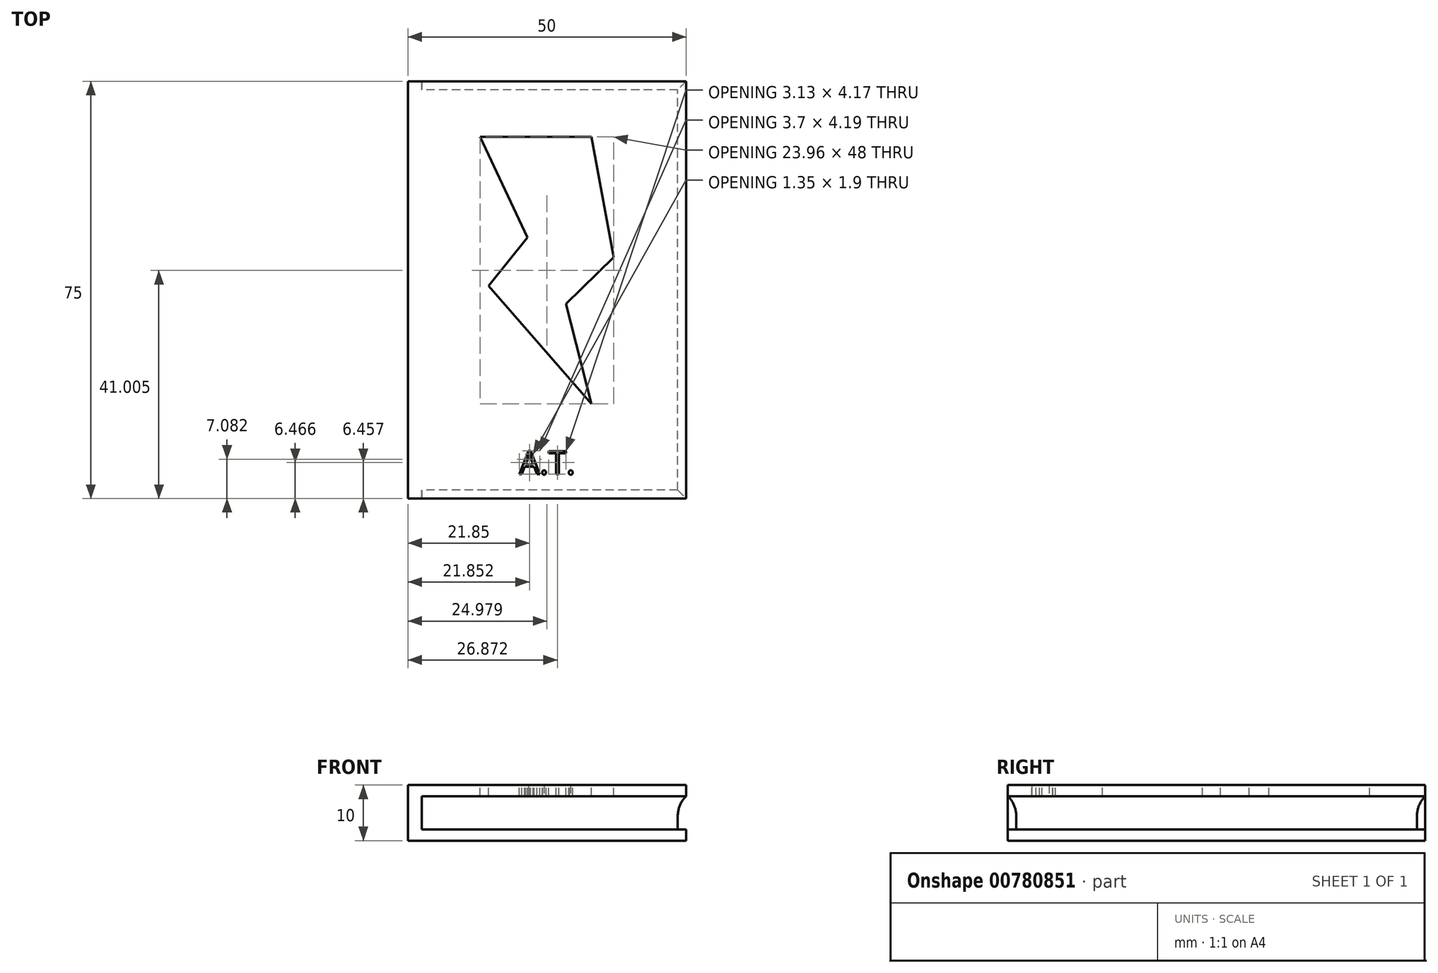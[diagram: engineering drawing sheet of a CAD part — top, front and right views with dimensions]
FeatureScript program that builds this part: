
annotation { "Feature Type Name" : "Feature", "Feature Type Description" : "" }
export const myFeature = defineFeature(function(context is Context, id is Id, definition is map)
    precondition{}
    {
        {
            var Q0;
            Q0=qCreatedBy(makeId("Top.planeOp"),FACE);
            var sketch = newSketch(context, id + "F0", { "sketchPlane" : qUnion([Q0])});
            skLineSegment(sketch, "E0.bottom", {"start": v(-61.42, 21.48) * mm, "end": v(-11.42, 21.48) * mm});
            skLineSegment(sketch, "E0.top", {"start": v(-61.42, -53.52) * mm, "end": v(-11.42, -53.52) * mm});
            skLineSegment(sketch, "E0.left", {"start": v(-61.42, 21.48) * mm, "end": v(-61.42, -53.52) * mm});
            skLineSegment(sketch, "E0.right", {"start": v(-11.42, 21.48) * mm, "end": v(-11.42, -53.52) * mm});
            skSolve(sketch);
        }
        {
            var Q0;
            Q0=makeQuery(id+"F0.imprint","IMPRINT",FACE,{"disambiguationData":[TD([[makeQuery(id+"F0.imprint","IMPRINT",EDGE,{"derivedFrom":sQuery(id+"F0.wireOp",EDGE,"E0.bottom")}),-1.0]])]});
            extrude(context, id + "F1", {"entities" : qUnion([Q0]), "depth" : 10 * mm, "offsetDistance" : 25 * mm});
        }
        {
            var Q0;
            Q0=makeQuery(id+"F1.opExtrude","SWEPT_FACE",FACE,{"disambiguationData":[OSD([sQuery(id+"F0.wireOp",EDGE,"E0.top")])]});
            var sketch = newSketch(context, id + "F2", { "sketchPlane" : qUnion([Q0])});
            skLineSegment(sketch, "E1.bottom", {"start": v(-58.92, 8) * mm, "end": v(-11.42, 8) * mm});
            skLineSegment(sketch, "E1.top", {"start": v(-58.92, 2) * mm, "end": v(-11.42, 2) * mm});
            skLineSegment(sketch, "E1.left", {"start": v(-58.92, 8) * mm, "end": v(-58.92, 2) * mm});
            skLineSegment(sketch, "E1.right", {"start": v(-11.42, 8) * mm, "end": v(-11.42, 2) * mm});
            skSolve(sketch);
        }
        {
            var Q0;
            Q0=makeQuery(id+"F1.opExtrude","SWEPT_FACE",FACE,{"disambiguationData":[OSD([sQuery(id+"F0.wireOp",EDGE,"E0.bottom")])]});
            var sketch = newSketch(context, id + "F3", { "sketchPlane" : qUnion([Q0])});
            skLineSegment(sketch, "E2.bottom", {"start": v(11.42, 8) * mm, "end": v(58.92, 8) * mm});
            skLineSegment(sketch, "E2.top", {"start": v(11.42, 2) * mm, "end": v(58.92, 2) * mm});
            skLineSegment(sketch, "E2.left", {"start": v(11.42, 8) * mm, "end": v(11.42, 2) * mm});
            skLineSegment(sketch, "E2.right", {"start": v(58.92, 8) * mm, "end": v(58.92, 2) * mm});
            skSolve(sketch);
        }
        {
            var Q0;
            Q0=makeQuery(id+"F1.opExtrude","SWEPT_FACE",FACE,{"disambiguationData":[OSD([sQuery(id+"F0.wireOp",EDGE,"E0.right")])]});
            var sketch = newSketch(context, id + "F4", { "sketchPlane" : qUnion([Q0])});
            skLineSegment(sketch, "E3.bottom", {"start": v(-53.52, 8) * mm, "end": v(21.48, 8) * mm});
            skLineSegment(sketch, "E3.top", {"start": v(-53.52, 2) * mm, "end": v(21.48, 2) * mm});
            skLineSegment(sketch, "E3.left", {"start": v(-53.52, 8) * mm, "end": v(-53.52, 2) * mm});
            skLineSegment(sketch, "E3.right", {"start": v(21.48, 8) * mm, "end": v(21.48, 2) * mm});
            skSolve(sketch);
        }
        {
            var Q0;
            Q0=makeQuery(id+"F2.imprint","IMPRINT",FACE,{"disambiguationData":[TD([[makeQuery(id+"F2.imprint","IMPRINT",EDGE,{"derivedFrom":sQuery(id+"F2.wireOp",EDGE,"E1.bottom")}),-1.0]])]});
            extrude(context, id + "F5", {"entities" : qUnion([Q0]), "operationType" : NewBodyOperationType.REMOVE, "oppositeDirection" : true, "depth" : 1.5 * mm, "offsetDistance" : 25 * mm});
        }
        {
            var Q0;
            Q0=makeQuery(id+"F4.imprint","IMPRINT",FACE,{"disambiguationData":[TD([[makeQuery(id+"F4.imprint","IMPRINT",EDGE,{"derivedFrom":sQuery(id+"F4.wireOp",EDGE,"E3.bottom")}),-1.0]])]});
            extrude(context, id + "F6", {"entities" : qUnion([Q0]), "operationType" : NewBodyOperationType.REMOVE, "oppositeDirection" : true, "depth" : 1.5 * mm, "offsetDistance" : 25 * mm});
        }
        {
            var Q0;
            Q0=makeQuery(id+"F3.imprint","IMPRINT",FACE,{"disambiguationData":[TD([[makeQuery(id+"F3.imprint","IMPRINT",EDGE,{"derivedFrom":sQuery(id+"F3.wireOp",EDGE,"E2.bottom")}),-1.0]])]});
            extrude(context, id + "F7", {"entities" : qUnion([Q0]), "operationType" : NewBodyOperationType.REMOVE, "oppositeDirection" : true, "depth" : 1.5 * mm, "offsetDistance" : 25 * mm});
        }
        {
            var Q0;
            Q0=makeQuery(id+"F1.opExtrude","CAP_FACE",FACE,{"disambiguationData":[OSD([sQuery(id+"F0.wireOp",EDGE,"E0.bottom"),sQuery(id+"F0.wireOp",EDGE,"E0.top"),sQuery(id+"F0.wireOp",EDGE,"E0.left"),sQuery(id+"F0.wireOp",EDGE,"E0.right")])],"isStart":false});
            var sketch = newSketch(context, id + "F8", { "sketchPlane" : qUnion([Q0])});
            skLineSegment(sketch, "E4", {"start": v(-48.42, 11.48) * mm, "end": v(-28.42, 11.48) * mm});
            skLineSegment(sketch, "E5", {"start": v(-28.42, 11.48) * mm, "end": v(-24.46, -10.16) * mm});
            skLineSegment(sketch, "E6", {"start": v(-24.46, -10.16) * mm, "end": v(-33.03, -18.53) * mm});
            skLineSegment(sketch, "E7", {"start": v(-33.03, -18.53) * mm, "end": v(-28.42, -36.52) * mm});
            skLineSegment(sketch, "E8", {"start": v(-28.42, -36.52) * mm, "end": v(-46.92, -15.3) * mm});
            skLineSegment(sketch, "E9", {"start": v(-46.92, -15.3) * mm, "end": v(-39.91, -6.62) * mm});
            skLineSegment(sketch, "E10", {"start": v(-39.91, -6.62) * mm, "end": v(-48.42, 11.48) * mm});
            skText(sketch, "E11", { "text": "A.T.", "fontName": "OpenSans-Regular.ttf"});
            const initialGuessF8  = {"E11": [-0.04142, -0.04915, 1, 0, 0.00421]};
            skSetInitialGuess(sketch, initialGuessF8);
            skSolve(sketch);
        }
        {
            var Q0;
            Q0 = qSketchRegion(id + "F8", true);
            extrude(context, id + "F9", {"entities" : qUnion([Q0]), "operationType" : NewBodyOperationType.REMOVE, "oppositeDirection" : true, "depth" : 2 * mm, "offsetDistance" : 25 * mm});
        }
        {
            var Q0;
            Q0=makeQuery(id+"F5.boolean.opBoolean","COPY",EDGE,{"derivedFrom":makeQuery(id+"F5.opExtrude","CAP_EDGE",EDGE,{"disambiguationData":[OSD([sQuery(id+"F2.wireOp",EDGE,"E1.bottom")])],"isStart":false})});
            var Q1;
            Q1=makeQuery(id+"F6.boolean.opBoolean","COPY",EDGE,{"derivedFrom":makeQuery(id+"F6.opExtrude","CAP_EDGE",EDGE,{"disambiguationData":[OSD([sQuery(id+"F4.wireOp",EDGE,"E3.bottom")])],"isStart":false})});
            var Q2;
            Q2=makeQuery(id+"F7.boolean.opBoolean","COPY",EDGE,{"derivedFrom":makeQuery(id+"F7.opExtrude","CAP_EDGE",EDGE,{"disambiguationData":[OSD([sQuery(id+"F3.wireOp",EDGE,"E2.bottom")])],"isStart":false})});
            fillet(context, id + "F10", {"entities" : qUnion([Q0, Q1, Q2]), "radius" : 5 * mm, "tangentPropagation" : true, "allowEdgeOverflow" : false});
        }
    });
